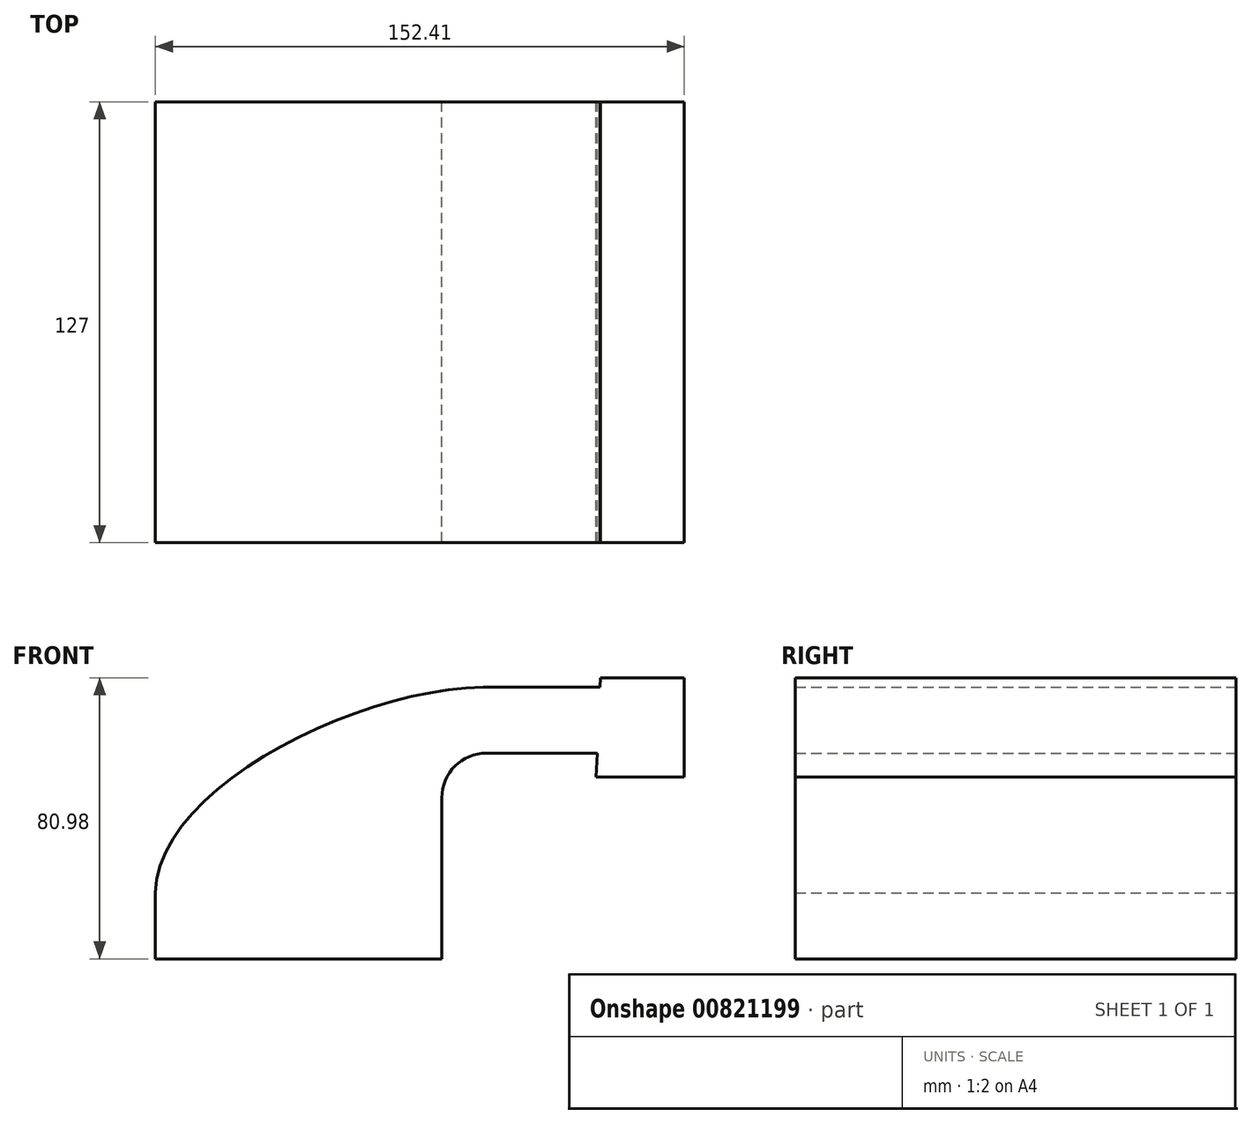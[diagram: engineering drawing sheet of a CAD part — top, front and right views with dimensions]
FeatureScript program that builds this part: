
annotation { "Feature Type Name" : "Feature", "Feature Type Description" : "" }
export const myFeature = defineFeature(function(context is Context, id is Id, definition is map)
    precondition{}
    {
        {
            var Q0;
            Q0=qCreatedBy(makeId("Front.planeOp"),FACE);
            var sketch = newSketch(context, id + "F0", { "sketchPlane" : qUnion([Q0])});
            skLineSegment(sketch, "E0.bottom", {"start": v(-41.28, 9.52) * mm, "end": v(41.27, 9.53) * mm});
            skLineSegment(sketch, "E0.top", {"start": v(-41.28, -9.53) * mm, "end": v(41.28, -9.53) * mm});
            skLineSegment(sketch, "E0.left", {"start": v(-41.28, 9.52) * mm, "end": v(-41.27, -9.53) * mm});
            skLineSegment(sketch, "E0.right", {"start": v(41.28, 9.53) * mm, "end": v(41.28, -9.52) * mm});
            skPoint(sketch, "E0.middle", {"position": v(0, 0) * mm});
            skLineSegment(sketch, "E1.bottom", {"start": v(60.32, 42.88) * mm, "end": v(111.12, 42.88) * mm});
            skLineSegment(sketch, "E1.top", {"start": v(60.32, 71.45) * mm, "end": v(111.12, 71.45) * mm});
            skLineSegment(sketch, "E1.left", {"start": v(60.32, 42.88) * mm, "end": v(60.32, 71.45) * mm});
            skLineSegment(sketch, "E1.right", {"start": v(111.12, 42.88) * mm, "end": v(111.12, 71.45) * mm});
            skPoint(sketch, "E1.middle", {"position": v(85.72, 57.16) * mm});
            skLineSegment(sketch, "E2", {"start": v(41.27, 9.53) * mm, "end": v(41.27, 36.9) * mm});
            skArc(sketch, "E3", {"start": v(41.27, 36.9) * mm, "mid": v(45.05, 46.01) * mm, "end": v(54.16, 49.78) * mm});
            skLineSegment(sketch, "E4", {"start": v(54.16, 49.78) * mm, "end": v(86.93, 49.78) * mm});
            skLineSegment(sketch, "E5.0", {"start": v(54.16, 68.83) * mm, "end": v(86.93, 68.83) * mm});
            skArc(sketch, "E5.1", {"start": v(22.23, 36.9) * mm, "mid": v(31.58, 59.48) * mm, "end": v(54.16, 68.83) * mm});
            skLineSegment(sketch, "E5.2", {"start": v(22.22, 9.53) * mm, "end": v(22.22, 36.9) * mm});
            skLineSegment(sketch, "E6", {"start": v(85.72, 42.88) * mm, "end": v(86.93, 71.45) * mm});
            skLineSegment(sketch, "E7", {"start": v(86.93, 71.45) * mm, "end": v(85.72, 42.88) * mm});
            skFitSpline(sketch, "E8", {"points": [v(-41.27, 9.52) * mm, v(54.16, 68.83) * mm], "startDerivative": vector(2.09, 91.7) * mm, "endDerivative": vector(110.64, 0.93) * mm});
            skSolve(sketch);
        }
        {
            var Q0;
            Q0=makeQuery(id+"F0.imprint","IMPRINT",FACE,{"disambiguationData":[TD([[makeQuery(id+"F0.imprint","IMPRINT",EDGE,{"derivedFrom":sQuery(id+"F0.wireOp",EDGE,"E0.top")}),1.0]])]});
            var Q1;
            {var subQ3=sQuery(id+"F0.wireOp",EDGE,"E5.2");Q1=makeQuery(id+"F0.imprint","IMPRINT",FACE,{"disambiguationData":[TD([[makeQuery(id+"F0.imprint","IMPRINT",EDGE,{"derivedFrom":subQ3}),1.0]])]});}
            var Q2;
            {var subQ1=sQuery(id+"F0.wireOp",EDGE,"E2");Q2=makeQuery(id+"F0.imprint","IMPRINT",FACE,{"disambiguationData":[TD([[makeQuery(id+"F0.imprint","IMPRINT",EDGE,{"derivedFrom":subQ1}),1.0]])]});}
            var Q3;
            {var subQ0=sQuery(id+"F0.wireOp",EDGE,"E4");var subQ1=sQuery(id+"F0.wireOp",EDGE,"E1.left");var subQ2=makeQuery(id+"F0.imprint","INTERSECT",VERTEX,{"derivedFrom":[subQ1,subQ0]});Q3=makeQuery(id+"F0.imprint","IMPRINT",FACE,{"disambiguationData":[TD([[makeQuery(id+"F0.imprint","IMPRINT",EDGE,{"disambiguationData":[TD([[subQ2,-1.0]])],"derivedFrom":subQ1}),-1.0]])]});}
            var Q4;
            {var subQ4=sQuery(id+"F0.wireOp",EDGE,"E1.right");Q4=makeQuery(id+"F0.imprint","IMPRINT",FACE,{"disambiguationData":[TD([[makeQuery(id+"F0.imprint","IMPRINT",EDGE,{"derivedFrom":subQ4}),1.0]])]});}
            extrude(context, id + "F1", {"entities" : qUnion([Q0, Q1, Q2, Q3, Q4]), "endBound" : BoundingType.SYMMETRIC, "depth" : 127 * mm, "offsetDistance" : 25.4 * mm});
        }
    });
